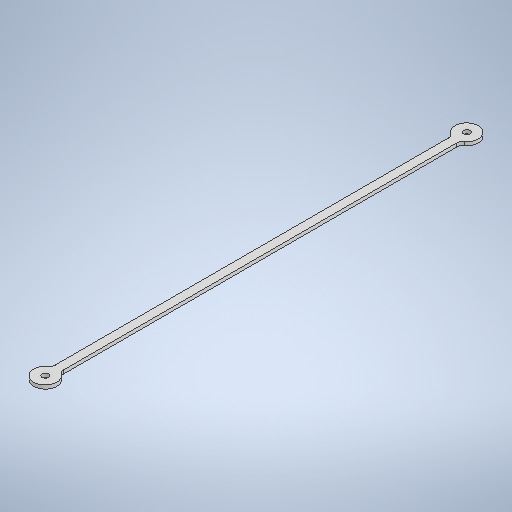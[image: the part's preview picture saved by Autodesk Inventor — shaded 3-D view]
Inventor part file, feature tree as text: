
AUTODESK INVENTOR PART (.ipt)
format: ipt  version: 2025.2 (Build 292293000, 293)  size: 282,624 bytes
history: native  units: in
note: dims shown in document units (in); Inventor stores cm internally (conversion verified against a paired STEP export)
features: extrude x2, sketch x2
ambient origin geometry x8: Origin, YZ Plane, XZ Plane, XY Plane, X Axis, Y Axis, Z Axis, Center Point
bodies: Solid1 (feature_tree)
feature tree (4):
  extrude  "Extrusion1"  Depth=0.1575in
  extrude  "Extrusion2"  Depth=0.0669in
  sketch  "Sketch1"  dims[d0=0.4291in d2=0.1575in]
  sketch  "Sketch2"  dims[d3=0.0787in d4=0.4291in d5=0.0787in d6=0.0in d7=7.874in d8=0.2756in d9=0.2756in d10=0.0in d11=0.0669in d12=0.0in d13=0.1181in d14=0.1181in d15=0.0669in d16=0.0in]
